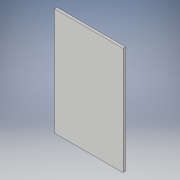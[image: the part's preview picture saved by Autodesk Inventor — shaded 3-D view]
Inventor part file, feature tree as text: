
AUTODESK INVENTOR PART (.ipt)
format: ipt  version: 2017 (Build 210142000, 142)  size: 88,576 bytes
history: native  units: in
note: dims shown in document units (in); Inventor stores cm internally (conversion verified against a paired STEP export)
features: extrude x1, sketch x1
ambient origin geometry x8: Origin, YZ Plane, XZ Plane, XY Plane, X Axis, Y Axis, Z Axis, Center Point
bodies: Solid1 (feature_tree)
feature tree (2):
  extrude  "Extrusion1"  Depth=11.0in
  sketch  "Sketch1"  dims[d0=7.0in d1=11.0in d2=0.25in d3=0.0in]
